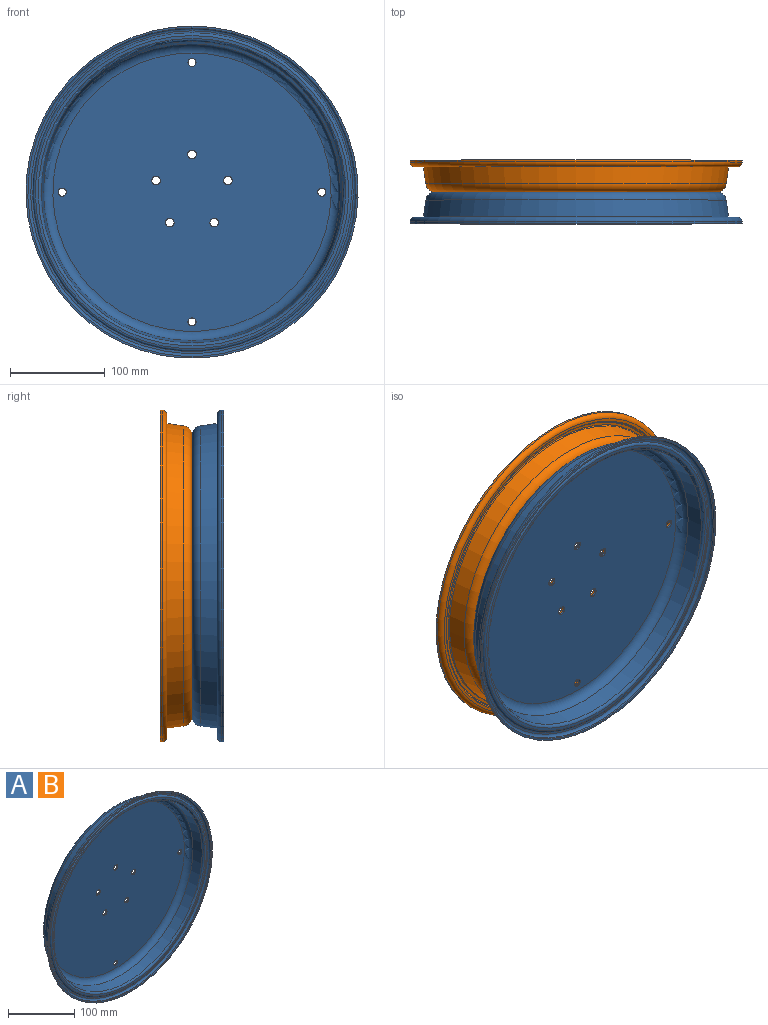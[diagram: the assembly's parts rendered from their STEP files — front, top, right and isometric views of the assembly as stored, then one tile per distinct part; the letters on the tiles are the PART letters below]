
ASSEMBLY  parts=2 mates=1
PART A: 29 faces, bbox 378.8x33.5x378.8 mm
  f0: plane 330x330mm, normal (0,-1,0), area 3081.9mm2, adj f1,f17
  f1: torus R=162mm, axis (0,1,0), area 4557mm2, adj f0,f2
  f2: cone r=155.27mm half-angle=8.3deg, axis (0,-1,0), area 17151.1mm2, adj f1,f18
  f3: plane 293.24x293.24mm, normal (0,-1,0), area 66990.3mm2, adj f18,f20,f21,f22,f23,f24,f25,f26
  f4: plane 296.7x296.7mm, normal (0,1,0), area 68593.6mm2, adj f19,f20,f21,f22,f23,f24,f25,f26
  f5: cone r=157mm half-angle=8.3deg, axis (0,-1,0), area 19194.9mm2, adj f6,f19
  f6: torus R=162mm, axis (0,1,0), area 1592.6mm2, adj f5,f7
  f7: plane 330x330mm, normal (0,1,0), area 3081.9mm2, adj f6,f8
  f8: torus R=165mm, axis (0,1,0), area 1634.8mm2, adj f7,f9
  f9: torus R=167mm, axis (0,1,0), area 1641.9mm2, adj f8,f10
  f10: plane 340x340mm, normal (0,1,0), area 3176.2mm2, adj f9,f11
  f11: torus R=170mm, axis (0,1,0), area 8546.2mm2, adj f10,f12
  f12: cylinder r=175mm len=350mm, axis (0,1,0), area 2199.1mm2, adj f11,f13
  f13: plane 350x350mm, normal (0,-1,0), area 2186.5mm2, adj f12,f14
  f14: cylinder r=173mm len=346mm, axis (0,1,0), area 2174mm2, adj f13,f15
  f15: torus R=170mm, axis (0,1,0), area 5090mm2, adj f14,f16
  f16: plane 340x340mm, normal (0,-1,0), area 2304.7mm2, adj f15,f17
  f17: torus R=165mm, axis (0,1,0), area 3866.2mm2, adj f0,f16
  f18: torus R=146.62mm, axis (0,1,0), area 13678mm2, adj f2,f3
  f19: torus R=148.35mm, axis (0,1,0), area 13833mm2, adj f4,f5
  f20: cylinder r=4.5mm len=9mm, axis (0,1,0), area 56.5mm2, adj f3,f4
  f21: cylinder r=4.5mm len=9mm, axis (0,1,0), area 56.5mm2, adj f3,f4
  f22: cylinder r=4.5mm len=9mm, axis (0,1,0), area 56.5mm2, adj f3,f4
  f23: cylinder r=4.5mm len=9mm, axis (0,1,0), area 56.5mm2, adj f3,f4
  f24: cylinder r=4.5mm len=9mm, axis (0,1,0), area 56.5mm2, adj f3,f4
  f25: cylinder r=4.25mm len=8.5mm, axis (0,1,0), area 53.4mm2, adj f3,f4
  f26: cylinder r=4.25mm len=8.5mm, axis (0,1,0), area 53.4mm2, adj f3,f4
  f27: cylinder r=4.25mm len=8.5mm, axis (0,1,0), area 53.4mm2, adj f3,f4
  f28: cylinder r=4.25mm len=8.5mm, axis (0,1,0), area 53.4mm2, adj f3,f4
PART B: same geometry as A
PLACE A t=(1.47,16.75,-0.49)mm
PLACE B rot(axis=(0,0,1),180deg) t=(1.47,16.75,-0.49)mm
MATE planar B.f1 <-> A.f1  axis (0,-1,0) through (1.47,16.75,-0.49)mm
